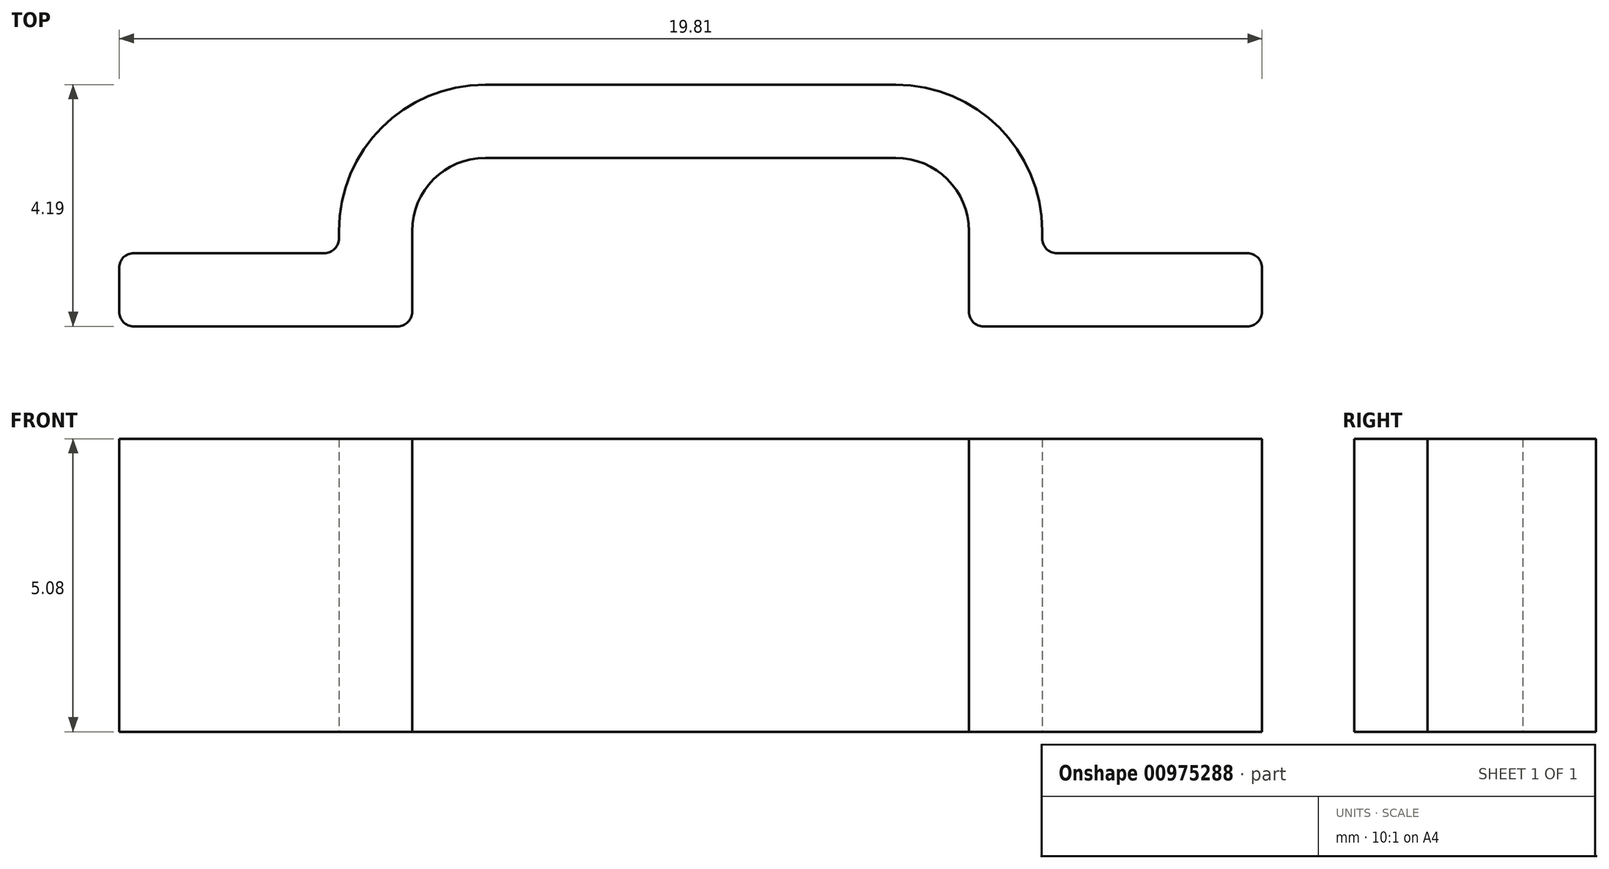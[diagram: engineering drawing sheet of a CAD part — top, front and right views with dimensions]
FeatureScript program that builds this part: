
annotation { "Feature Type Name" : "Feature", "Feature Type Description" : "" }
export const myFeature = defineFeature(function(context is Context, id is Id, definition is map)
    precondition{}
    {
        {
            var Q0;
            Q0=qCreatedBy(makeId("Top.planeOp"),FACE);
            var sketch = newSketch(context, id + "F0", { "sketchPlane" : qUnion([Q0])});
            skLineSegment(sketch, "E0.bottom", {"start": v(-47.16, 9.12) * mm, "end": v(-40.05, 9.12) * mm});
            skLineSegment(sketch, "E0.right", {"start": v(-38.78, 7.85) * mm, "end": v(-38.78, 6.45) * mm});
            skPoint(sketch, "E1.visualSharp", {"position": v(-48.43, 9.12) * mm});
            skPoint(sketch, "E2.visualSharp", {"position": v(-38.78, 9.12) * mm});
            skArc(sketch, "E2.filletArc", {"start": v(-38.78, 7.85) * mm, "mid": v(-39.15, 8.75) * mm, "end": v(-40.05, 9.12) * mm});
            skLineSegment(sketch, "E3", {"start": v(-38.53, 6.2) * mm, "end": v(-33.96, 6.2) * mm});
            skLineSegment(sketch, "E4.0", {"start": v(-37.26, 7.47) * mm, "end": v(-33.96, 7.47) * mm});
            skLineSegment(sketch, "E4.1", {"start": v(-37.51, 7.85) * mm, "end": v(-37.51, 7.72) * mm});
            skArc(sketch, "E4.2", {"start": v(-37.51, 7.85) * mm, "mid": v(-38.26, 9.65) * mm, "end": v(-40.05, 10.39) * mm});
            skLineSegment(sketch, "E4.3", {"start": v(-47.16, 10.39) * mm, "end": v(-40.05, 10.39) * mm});
            skLineSegment(sketch, "E5", {"start": v(-33.7, 7.21) * mm, "end": v(-33.7, 6.45) * mm});
            skPoint(sketch, "E6.visualSharp", {"position": v(-37.51, 7.47) * mm});
            skArc(sketch, "E6.filletArc", {"start": v(-37.51, 7.72) * mm, "mid": v(-37.44, 7.54) * mm, "end": v(-37.26, 7.47) * mm});
            skPoint(sketch, "E7.visualSharp", {"position": v(-33.7, 7.47) * mm});
            skArc(sketch, "E7.filletArc", {"start": v(-33.7, 7.21) * mm, "mid": v(-33.78, 7.4) * mm, "end": v(-33.96, 7.47) * mm});
            skPoint(sketch, "E8.visualSharp", {"position": v(-38.78, 6.2) * mm});
            skArc(sketch, "E8.filletArc", {"start": v(-38.78, 6.45) * mm, "mid": v(-38.7, 6.27) * mm, "end": v(-38.53, 6.2) * mm});
            skPoint(sketch, "E9.visualSharp", {"position": v(-33.7, 6.2) * mm});
            skArc(sketch, "E9.filletArc", {"start": v(-33.96, 6.2) * mm, "mid": v(-33.78, 6.27) * mm, "end": v(-33.7, 6.45) * mm});
            skPoint(sketch, "E10", {"position": v(-43.6, 10.39) * mm});
            skLineSegment(sketch, "E11", {"start": v(-43.6, 10.39) * mm, "end": v(-43.6, 17.4) * mm, "construction": true});
            skLineSegment(sketch, "E12.MirrorCS", {"start": v(-49.7, 7.85) * mm, "end": v(-49.7, 7.72) * mm});
            skArc(sketch, "E13.MirrorCS", {"start": v(-53.26, 6.2) * mm, "mid": v(-53.44, 6.27) * mm, "end": v(-53.51, 6.45) * mm});
            skArc(sketch, "E14.MirrorCS", {"start": v(-53.51, 7.21) * mm, "mid": v(-53.44, 7.4) * mm, "end": v(-53.26, 7.47) * mm});
            skArc(sketch, "E15.MirrorCS", {"start": v(-48.43, 6.45) * mm, "mid": v(-48.5, 6.27) * mm, "end": v(-48.69, 6.2) * mm});
            skArc(sketch, "E16.MirrorCS", {"start": v(-49.7, 7.72) * mm, "mid": v(-49.78, 7.54) * mm, "end": v(-49.96, 7.47) * mm});
            skLineSegment(sketch, "E17.MirrorCS", {"start": v(-48.69, 6.2) * mm, "end": v(-53.26, 6.2) * mm});
            skPoint(sketch, "E18.MirrorP", {"position": v(-48.43, 6.2) * mm});
            skPoint(sketch, "E19.MirrorP", {"position": v(-49.7, 7.47) * mm});
            skArc(sketch, "E20.MirrorCS", {"start": v(-48.43, 7.85) * mm, "mid": v(-48.06, 8.75) * mm, "end": v(-47.16, 9.12) * mm});
            skPoint(sketch, "E21.MirrorP", {"position": v(-53.51, 6.2) * mm});
            skArc(sketch, "E22.MirrorCS", {"start": v(-49.7, 7.85) * mm, "mid": v(-48.96, 9.65) * mm, "end": v(-47.16, 10.39) * mm});
            skLineSegment(sketch, "E23.MirrorCS", {"start": v(-53.51, 7.21) * mm, "end": v(-53.51, 6.45) * mm});
            skLineSegment(sketch, "E24.MirrorCS", {"start": v(-48.43, 7.85) * mm, "end": v(-48.43, 6.45) * mm});
            skLineSegment(sketch, "E25.MirrorCS", {"start": v(-49.96, 7.47) * mm, "end": v(-53.26, 7.47) * mm});
            skPoint(sketch, "E26.MirrorP", {"position": v(-53.51, 7.47) * mm});
            skSolve(sketch);
        }
        {
            var Q0;
            Q0=makeQuery(id+"F0.imprint","IMPRINT",FACE,{"disambiguationData":[TD([[makeQuery(id+"F0.imprint","IMPRINT",EDGE,{"derivedFrom":sQuery(id+"F0.wireOp",EDGE,"E0.bottom")}),1.0]])]});
            extrude(context, id + "F1", {"entities" : qUnion([Q0]), "depth" : 5.08 * mm, "offsetDistance" : 25.4 * mm});
        }
    });
